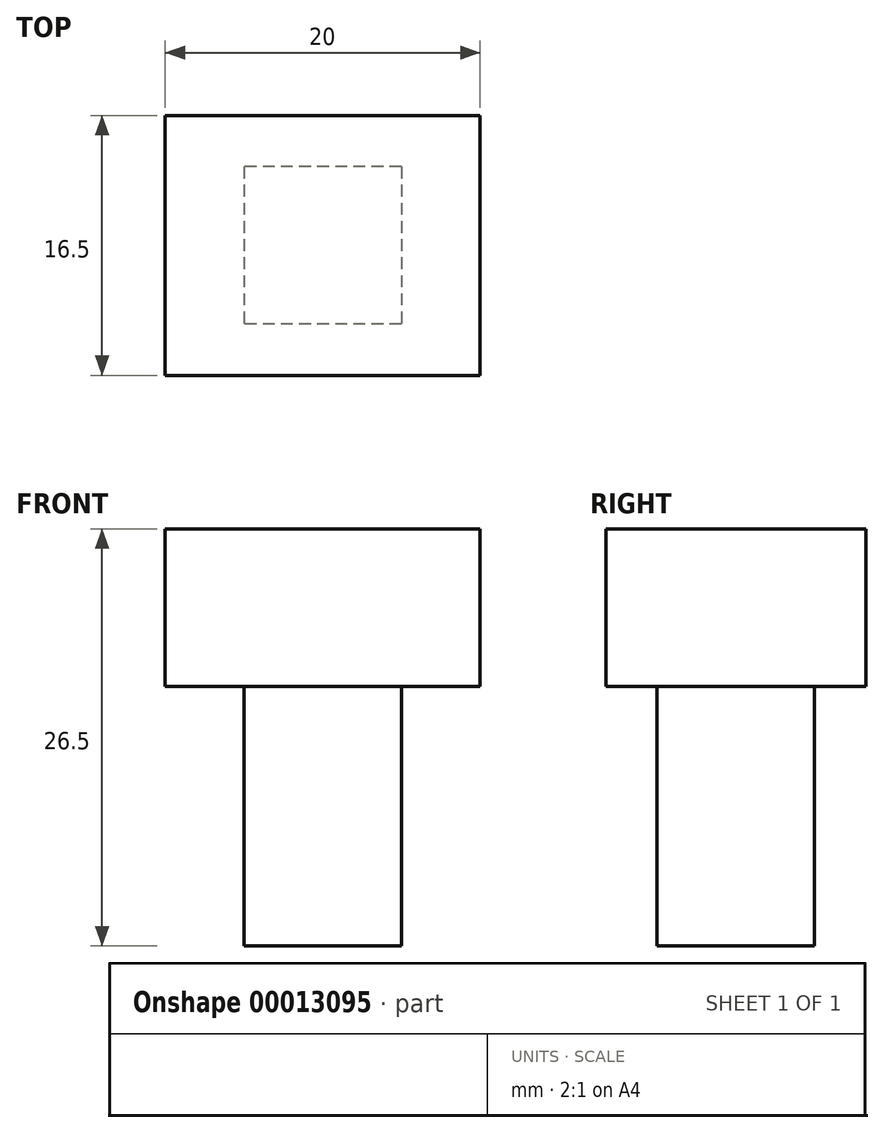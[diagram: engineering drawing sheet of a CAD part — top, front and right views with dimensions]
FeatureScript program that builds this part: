
annotation { "Feature Type Name" : "Feature", "Feature Type Description" : "" }
export const myFeature = defineFeature(function(context is Context, id is Id, definition is map)
    precondition{}
    {
        {
            var Q0;
            Q0=qCreatedBy(makeId("Top.planeOp"),FACE);
            var sketch = newSketch(context, id + "F0", { "sketchPlane" : qUnion([Q0])});
            skLineSegment(sketch, "E0.bottom", {"start": v(-60.35, 41.85) * mm, "end": v(-40.35, 41.85) * mm});
            skLineSegment(sketch, "E0.top", {"start": v(-60.35, 25.35) * mm, "end": v(-40.35, 25.35) * mm});
            skLineSegment(sketch, "E0.left", {"start": v(-60.35, 41.85) * mm, "end": v(-60.35, 25.35) * mm});
            skLineSegment(sketch, "E0.right", {"start": v(-40.35, 41.85) * mm, "end": v(-40.35, 25.35) * mm});
            skSolve(sketch);
        }
        {
            var Q0;
            Q0=makeQuery(id+"F0.imprint","IMPRINT",FACE,{"disambiguationData":[TD([[makeQuery(id+"F0.imprint","IMPRINT",EDGE,{"derivedFrom":sQuery(id+"F0.wireOp",EDGE,"E0.bottom")}),-1.0]])]});
            extrude(context, id + "F1", {"entities" : qUnion([Q0]), "depth" : 10 * mm});
        }
        {
            var Q0;
            Q0=makeQuery(id+"F1.opExtrude","CAP_FACE",FACE,{"disambiguationData":[OSD([sQuery(id+"F0.wireOp",EDGE,"E0.bottom"),sQuery(id+"F0.wireOp",EDGE,"E0.top"),sQuery(id+"F0.wireOp",EDGE,"E0.left"),sQuery(id+"F0.wireOp",EDGE,"E0.right")])],"isStart":true});
            var sketch = newSketch(context, id + "F2", { "sketchPlane" : qUnion([Q0])});
            skLineSegment(sketch, "E1.0", {"start": v(-60.35, -41.85) * mm, "end": v(-60.35, -25.35) * mm});
            skLineSegment(sketch, "E2.0", {"start": v(-60.35, -25.35) * mm, "end": v(-40.35, -25.35) * mm});
            skLineSegment(sketch, "E3.0", {"start": v(-40.35, -41.85) * mm, "end": v(-40.35, -25.35) * mm});
            skLineSegment(sketch, "E4.0", {"start": v(-60.35, -41.85) * mm, "end": v(-40.35, -41.85) * mm});
            skLineSegment(sketch, "E5", {"start": v(-60.35, -33.6) * mm, "end": v(-40.35, -33.6) * mm, "construction": true});
            skLineSegment(sketch, "E6", {"start": v(-50.35, -25.35) * mm, "end": v(-50.35, -41.85) * mm, "construction": true});
            skLineSegment(sketch, "E7.rect.bottom", {"start": v(-45.35, -38.6) * mm, "end": v(-55.35, -38.6) * mm});
            skLineSegment(sketch, "E7.rect.top", {"start": v(-45.35, -28.6) * mm, "end": v(-55.35, -28.6) * mm});
            skLineSegment(sketch, "E7.rect.left", {"start": v(-45.35, -38.6) * mm, "end": v(-45.35, -28.6) * mm});
            skLineSegment(sketch, "E7.rect.right", {"start": v(-55.35, -38.6) * mm, "end": v(-55.35, -28.6) * mm});
            skPoint(sketch, "E7.rect.middle", {"position": v(-50.35, -33.6) * mm});
            skSolve(sketch);
        }
        {
            var Q0;
            Q0=makeQuery(id+"F2.imprint","IMPRINT",FACE,{"disambiguationData":[TD([[makeQuery(id+"F2.imprint","IMPRINT",EDGE,{"derivedFrom":sQuery(id+"F2.wireOp",EDGE,"E7.rect.bottom")}),-1.0]])]});
            extrude(context, id + "F3", {"entities" : qUnion([Q0]), "operationType" : NewBodyOperationType.ADD, "depth" : 16.5 * mm});
        }
    });
